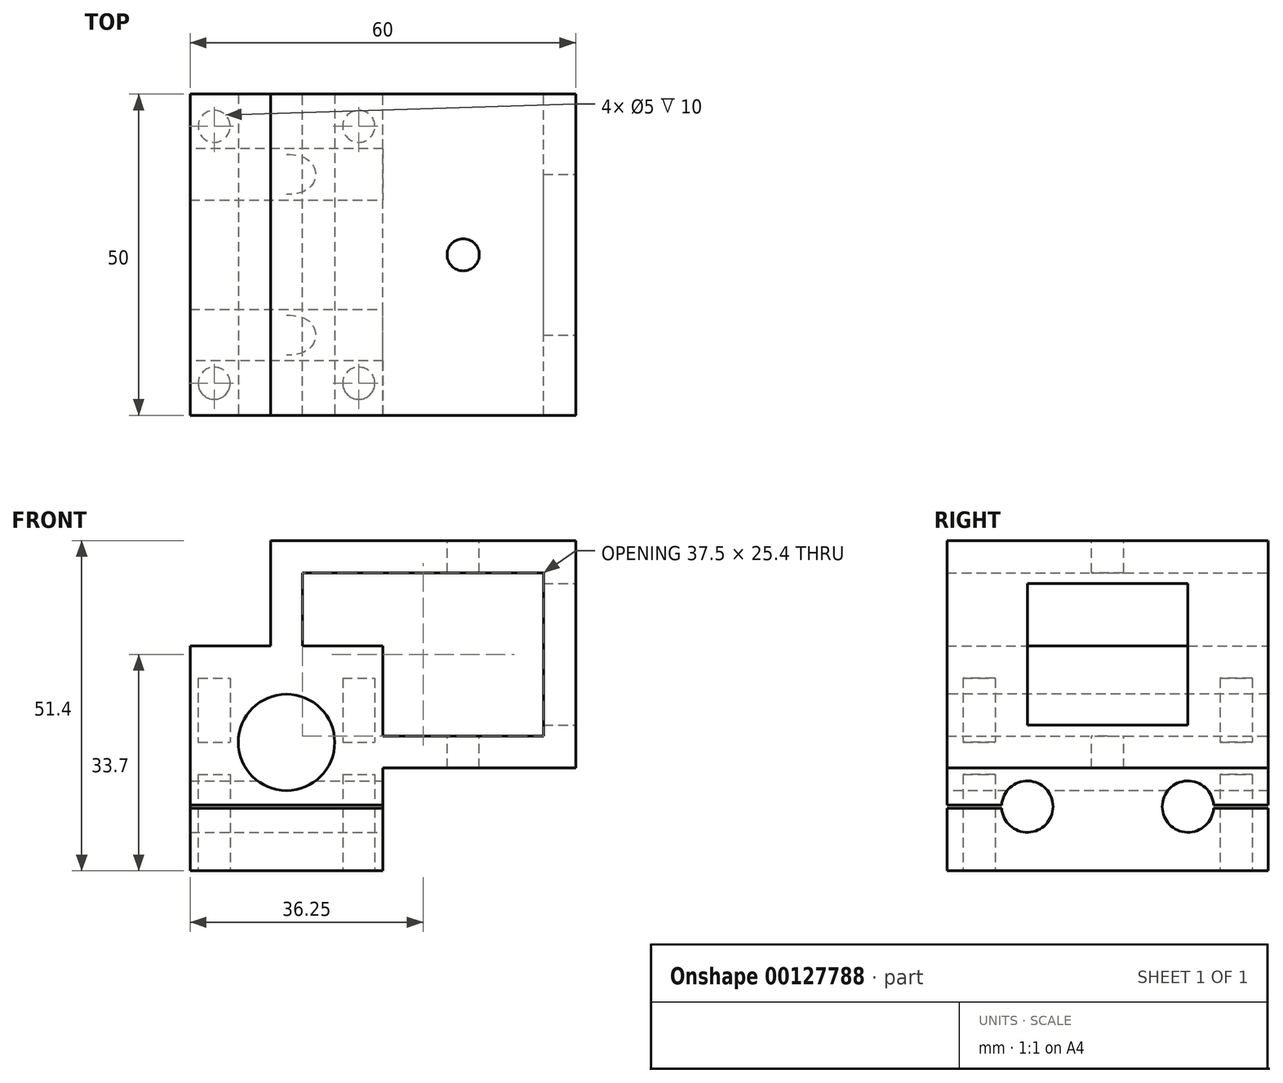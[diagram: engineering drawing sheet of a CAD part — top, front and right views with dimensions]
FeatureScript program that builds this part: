
annotation { "Feature Type Name" : "Feature", "Feature Type Description" : "" }
export const myFeature = defineFeature(function(context is Context, id is Id, definition is map)
    precondition{}
    {
        {
            var Q0;
            Q0=qCreatedBy(makeId("Front.planeOp"),FACE);
            var sketch = newSketch(context, id + "F0", { "sketchPlane" : qUnion([Q0])});
            skLineSegment(sketch, "E0.bottom", {"start": v(15, 0) * mm, "end": v(-15, 0) * mm});
            skLineSegment(sketch, "E0.right", {"start": v(-15, 0) * mm, "end": v(-15, 15) * mm});
            skPoint(sketch, "E0.middle", {"position": v(0, 0) * mm});
            skLineSegment(sketch, "E1", {"start": v(-15, 15) * mm, "end": v(15, 15) * mm});
            skLineSegment(sketch, "E2", {"start": v(15, 0) * mm, "end": v(15, 15) * mm});
            skSolve(sketch);
        }
        {
            var Q0;
            Q0 = qSketchRegion(id + "F0", true);
            extrude(context, id + "F1", {"entities" : qUnion([Q0]), "endBound" : BoundingType.SYMMETRIC, "depth" : 50 * mm});
        }
        {
            var Q0;
            Q0=makeQuery(id+"F1.opExtrude","CAP_FACE",FACE,{"disambiguationData":[OSD([sQuery(id+"F0.wireOp",EDGE,"E0.bottom"),sQuery(id+"F0.wireOp",EDGE,"E0.top"),sQuery(id+"F0.wireOp",EDGE,"E0.left"),sQuery(id+"F0.wireOp",EDGE,"E0.right")])],"isStart":false});
            var sketch = newSketch(context, id + "F2", { "sketchPlane" : qUnion([Q0])});
            skCircle(sketch, "E3", {"center": v(0, 0) * mm, "radius": 7.5 * mm});
            skSolve(sketch);
        }
        {
            var Q0;
            Q0 = qSketchRegion(id + "F2", true);
            extrude(context, id + "F3", {"entities" : qUnion([Q0]), "operationType" : NewBodyOperationType.REMOVE, "endBound" : BoundingType.THROUGH_ALL, "oppositeDirection" : true, "depth" : 25 * mm});
        }
        {
            var Q0;
            {var subQ2=sQuery(id+"F0.wireOp",EDGE,"E0.right");var subQ5=sQuery(id+"F0.wireOp",EDGE,"E0.bottom");Q0=makeQuery(id+"F3.boolean.opBoolean","SPLIT",FACE,{"disambiguationData":[TD([makeQuery(id+"F1.opExtrude","SWEPT_FACE",FACE,{"disambiguationData":[OSD([subQ2])]})])],"derivedFrom":makeQuery(id+"F1.opExtrude","SWEPT_FACE",FACE,{"disambiguationData":[OSD([subQ5])]})});}
            var sketch = newSketch(context, id + "F4", { "sketchPlane" : qUnion([Q0])});
            skCircle(sketch, "E4", {"center": v(-11.25, 20) * mm, "radius": 2.5 * mm});
            skLineSegment(sketch, "E5", {"start": v(0, 0) * mm, "end": v(-45.22, 0) * mm, "construction": true});
            skLineSegment(sketch, "E6", {"start": v(-11.25, 20) * mm, "end": v(-11.25, 25) * mm, "construction": true});
            skCircle(sketch, "E7.MirrorC", {"center": v(-11.25, -20) * mm, "radius": 2.5 * mm});
            skLineSegment(sketch, "E8", {"start": v(-7.5, 25) * mm, "end": v(7.5, 25) * mm, "construction": true});
            skLineSegment(sketch, "E9", {"start": v(0, 25) * mm, "end": v(0, -34.32) * mm, "construction": true});
            skCircle(sketch, "E10.MirrorC", {"center": v(11.25, 20) * mm, "radius": 2.5 * mm});
            skCircle(sketch, "E11.MirrorC", {"center": v(11.25, -20) * mm, "radius": 2.5 * mm});
            skSolve(sketch);
        }
        {
            var Q0;
            Q0 = qSketchRegion(id + "F4", true);
            extrude(context, id + "F5", {"entities" : qUnion([Q0]), "operationType" : NewBodyOperationType.REMOVE, "oppositeDirection" : true, "depth" : 10 * mm});
        }
        {
            var Q0;
            {var subQ2=sQuery(id+"F0.wireOp",EDGE,"E0.right");var subQ5=sQuery(id+"F0.wireOp",EDGE,"E0.bottom");Q0=makeQuery(id+"F3.boolean.opBoolean","SPLIT",FACE,{"disambiguationData":[TD([makeQuery(id+"F1.opExtrude","SWEPT_FACE",FACE,{"disambiguationData":[OSD([subQ2])]})])],"derivedFrom":makeQuery(id+"F1.opExtrude","SWEPT_FACE",FACE,{"disambiguationData":[OSD([subQ5])]})});}
            var sketch = newSketch(context, id + "F6", { "sketchPlane" : qUnion([Q0])});
            skLineSegment(sketch, "E12.bottom", {"start": v(-15, 25) * mm, "end": v(15, 25) * mm});
            skLineSegment(sketch, "E12.top", {"start": v(-15, -25) * mm, "end": v(15, -25) * mm});
            skLineSegment(sketch, "E12.left", {"start": v(-15, 25) * mm, "end": v(-15, -25) * mm});
            skLineSegment(sketch, "E12.right", {"start": v(15, 25) * mm, "end": v(15, -25) * mm});
            skSolve(sketch);
        }
        {
            var Q0;
            Q0 = qSketchRegion(id + "F6", true);
            extrude(context, id + "F7", {"entities" : qUnion([Q0]), "depth" : 20 * mm});
        }
        {
            var Q0;
            Q0=makeQuery(id+"F7.opExtrude","SWEPT_FACE",FACE,{"disambiguationData":[OSD([sQuery(id+"F6.wireOp",EDGE,"E12.bottom")])]});
            var sketch = newSketch(context, id + "F8", { "sketchPlane" : qUnion([Q0])});
            skCircle(sketch, "E13", {"center": v(0, 0) * mm, "radius": 7.5 * mm});
            skSolve(sketch);
        }
        {
            var Q0;
            Q0 = qSketchRegion(id + "F8", true);
            extrude(context, id + "F9", {"entities" : qUnion([Q0]), "operationType" : NewBodyOperationType.REMOVE, "endBound" : BoundingType.THROUGH_ALL, "oppositeDirection" : true, "depth" : 25 * mm});
        }
        {
            var Q0;
            Q0=makeQuery(id+"F7.opExtrude","CAP_FACE",FACE,{"disambiguationData":[OSD([sQuery(id+"F6.wireOp",EDGE,"E12.bottom"),sQuery(id+"F6.wireOp",EDGE,"E12.top"),sQuery(id+"F6.wireOp",EDGE,"E12.left"),sQuery(id+"F6.wireOp",EDGE,"E12.right")])],"isStart":false});
            var sketch = newSketch(context, id + "F10", { "sketchPlane" : qUnion([Q0])});
            skCircle(sketch, "E14.0", {"center": v(-11.25, 20) * mm, "radius": 2.5 * mm});
            skCircle(sketch, "E15.0", {"center": v(11.25, 20) * mm, "radius": 2.5 * mm});
            skCircle(sketch, "E16.0", {"center": v(11.25, -20) * mm, "radius": 2.5 * mm});
            skCircle(sketch, "E17.0", {"center": v(-11.25, -20) * mm, "radius": 2.5 * mm});
            skSolve(sketch);
        }
        {
            var Q0;
            Q0 = qSketchRegion(id + "F10", true);
            var Q1;
            Q1=makeQuery(id+"F1.opExtrude","SWEPT_BODY",BODY,{"disambiguationData":[OSD([sQuery(id+"F0.wireOp",EDGE,"E0.bottom"),sQuery(id+"F0.wireOp",EDGE,"E0.top"),sQuery(id+"F0.wireOp",EDGE,"E0.left"),sQuery(id+"F0.wireOp",EDGE,"E0.right"),sQuery(id+"F0.wireOp",EDGE,"E1"),sQuery(id+"F0.wireOp",EDGE,"E2")])]});
            extrude(context, id + "F11", {"entities" : qUnion([Q0]), "operationType" : NewBodyOperationType.REMOVE, "oppositeDirection" : true, "endBoundEntityBody" : qUnion([Q1]), "depth" : 15 * mm});
        }
        {
            var Q0;
            Q0=makeQuery(id+"F7.opExtrude","SWEPT_FACE",FACE,{"disambiguationData":[OSD([sQuery(id+"F6.wireOp",EDGE,"E12.right")])]});
            var sketch = newSketch(context, id + "F12", { "sketchPlane" : qUnion([Q0])});
            skCircle(sketch, "E18", {"center": v(-12.5, -10) * mm, "radius": 4 * mm});
            skCircle(sketch, "E19", {"center": v(12.5, -10) * mm, "radius": 4 * mm});
            skLineSegment(sketch, "E20", {"start": v(0, 0) * mm, "end": v(0, -20) * mm, "construction": true});
            skLineSegment(sketch, "E21", {"start": v(-12.5, -10) * mm, "end": v(0, -10) * mm, "construction": true});
            skSolve(sketch);
        }
        {
            var Q0;
            Q0 = qSketchRegion(id + "F12", true);
            extrude(context, id + "F13", {"entities" : qUnion([Q0]), "operationType" : NewBodyOperationType.REMOVE, "endBound" : BoundingType.THROUGH_ALL, "oppositeDirection" : true, "depth" : 25 * mm});
        }
        {
            var Q0;
            Q0=makeQuery(id+"F7.opExtrude","SWEPT_FACE",FACE,{"disambiguationData":[OSD([sQuery(id+"F6.wireOp",EDGE,"E12.left")])]});
            var sketch = newSketch(context, id + "F14", { "sketchPlane" : qUnion([Q0])});
            skLineSegment(sketch, "E22", {"start": v(0, 0) * mm, "end": v(0, -20) * mm, "construction": true});
            skLineSegment(sketch, "E23", {"start": v(-25, -9.75) * mm, "end": v(-16.5, -9.75) * mm});
            skArc(sketch, "E24.0", {"start": v(-16.5, -9.75) * mm, "mid": v(-16.5, -10) * mm, "end": v(-16.5, -10.25) * mm});
            skLineSegment(sketch, "E25", {"start": v(-25, -10.25) * mm, "end": v(-16.5, -10.25) * mm});
            skLineSegment(sketch, "E26", {"start": v(0, -10) * mm, "end": v(-11.5, -10) * mm, "construction": true});
            skLineSegment(sketch, "E27", {"start": v(-25, -9.75) * mm, "end": v(-25, -10.25) * mm});
            skLineSegment(sketch, "E28.MirrorCS", {"start": v(25, -9.75) * mm, "end": v(25, -10.25) * mm});
            skArc(sketch, "E29.MirrorCS", {"start": v(16.5, -9.75) * mm, "mid": v(16.5, -10) * mm, "end": v(16.5, -10.25) * mm});
            skLineSegment(sketch, "E30.MirrorCS", {"start": v(25, -10.25) * mm, "end": v(16.5, -10.25) * mm});
            skLineSegment(sketch, "E31.MirrorCS", {"start": v(25, -9.75) * mm, "end": v(16.5, -9.75) * mm});
            skSolve(sketch);
        }
        {
            var Q0;
            Q0 = qSketchRegion(id + "F14", true);
            extrude(context, id + "F15", {"entities" : qUnion([Q0]), "operationType" : NewBodyOperationType.REMOVE, "endBound" : BoundingType.THROUGH_ALL, "oppositeDirection" : true, "depth" : 25 * mm});
        }
        {
            var Q0;
            Q0=qCreatedBy(makeId("Front.planeOp"),FACE);
            var sketch = newSketch(context, id + "F16", { "sketchPlane" : qUnion([Q0])});
            skLineSegment(sketch, "E32", {"start": v(15, -4) * mm, "end": v(45, -4) * mm});
            skLineSegment(sketch, "E33", {"start": v(45, -4) * mm, "end": v(45, 31.4) * mm});
            skLineSegment(sketch, "E34", {"start": v(45, 31.4) * mm, "end": v(-2.5, 31.4) * mm});
            skLineSegment(sketch, "E35", {"start": v(-2.5, 31.4) * mm, "end": v(-2.5, 15) * mm});
            skLineSegment(sketch, "E36", {"start": v(-2.5, 15) * mm, "end": v(2.5, 15) * mm});
            skLineSegment(sketch, "E37", {"start": v(2.5, 15) * mm, "end": v(2.5, 26.4) * mm});
            skLineSegment(sketch, "E38", {"start": v(2.5, 26.4) * mm, "end": v(40, 26.4) * mm});
            skLineSegment(sketch, "E39", {"start": v(40, 26.4) * mm, "end": v(40, 1) * mm});
            skLineSegment(sketch, "E40", {"start": v(40, 1) * mm, "end": v(15, 1) * mm});
            skLineSegment(sketch, "E41", {"start": v(15, 1) * mm, "end": v(15, -4) * mm});
            skLineSegment(sketch, "E42", {"start": v(0, 0) * mm, "end": v(0, 15) * mm, "construction": true});
            skSolve(sketch);
        }
        {
            var Q0;
            Q0=makeQuery(id+"F16.imprint","IMPRINT",FACE,{"disambiguationData":[TD([[makeQuery(id+"F16.imprint","IMPRINT",EDGE,{"derivedFrom":sQuery(id+"F16.wireOp",EDGE,"E32")}),1.0]])]});
            extrude(context, id + "F17", {"entities" : qUnion([Q0]), "operationType" : NewBodyOperationType.ADD, "endBound" : BoundingType.SYMMETRIC, "depth" : 50 * mm});
        }
        {
            var Q0;
            Q0=makeQuery(id+"F17.opExtrude","SWEPT_FACE",FACE,{"disambiguationData":[OSD([sQuery(id+"F16.wireOp",EDGE,"E40")])]});
            var sketch = newSketch(context, id + "F18", { "sketchPlane" : qUnion([Q0])});
            skCircle(sketch, "E43", {"center": v(27.5, 0) * mm, "radius": 2.5 * mm});
            skLineSegment(sketch, "E44", {"start": v(27.5, 25) * mm, "end": v(27.5, -25) * mm, "construction": true});
            skSolve(sketch);
        }
        {
            var Q0;
            Q0 = qSketchRegion(id + "F18", true);
            extrude(context, id + "F19", {"entities" : qUnion([Q0]), "operationType" : NewBodyOperationType.REMOVE, "endBound" : BoundingType.THROUGH_ALL, "oppositeDirection" : true, "depth" : 50 * mm, "hasSecondDirection" : true, "secondDirectionBound" : SecondDirectionBoundingType.THROUGH_ALL, "secondDirectionOppositeDirection" : false, "secondDirectionDepth" : 25 * mm});
        }
        {
            var Q0;
            Q0=makeQuery(id+"F17.opExtrude","SWEPT_FACE",FACE,{"disambiguationData":[OSD([sQuery(id+"F16.wireOp",EDGE,"E33")])]});
            var sketch = newSketch(context, id + "F20", { "sketchPlane" : qUnion([Q0])});
            skLineSegment(sketch, "E45.bottom", {"start": v(12.5, 2.7) * mm, "end": v(-12.5, 2.7) * mm});
            skLineSegment(sketch, "E45.top", {"start": v(12.5, 24.7) * mm, "end": v(-12.5, 24.7) * mm});
            skLineSegment(sketch, "E45.left", {"start": v(12.5, 2.7) * mm, "end": v(12.5, 24.7) * mm});
            skLineSegment(sketch, "E45.right", {"start": v(-12.5, 2.7) * mm, "end": v(-12.5, 24.7) * mm});
            skPoint(sketch, "E45.middle", {"position": v(0, 13.7) * mm});
            skLineSegment(sketch, "E46", {"start": v(25, 13.7) * mm, "end": v(-25, 13.7) * mm, "construction": true});
            skSolve(sketch);
        }
        {
            var Q0;
            Q0=makeQuery(id+"F20.imprint","IMPRINT",FACE,{"disambiguationData":[TD([[makeQuery(id+"F20.imprint","IMPRINT",EDGE,{"derivedFrom":sQuery(id+"F20.wireOp",EDGE,"E45.bottom")}),-1.0]])]});
            extrude(context, id + "F21", {"entities" : qUnion([Q0]), "operationType" : NewBodyOperationType.REMOVE, "endBound" : BoundingType.UP_TO_NEXT, "oppositeDirection" : true, "depth" : 25 * mm});
        }
    });
